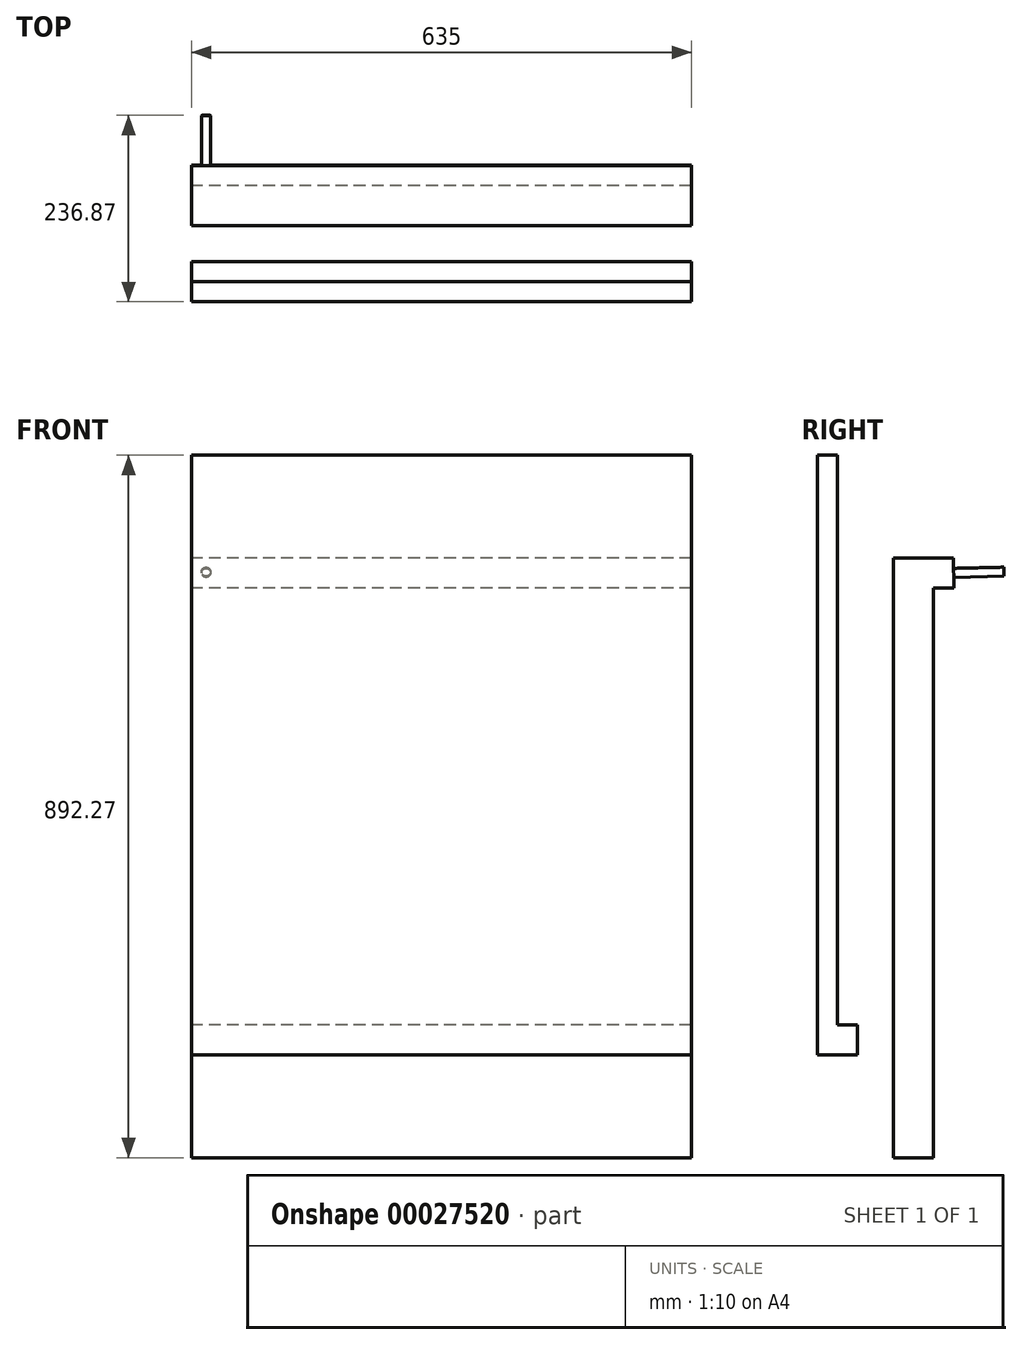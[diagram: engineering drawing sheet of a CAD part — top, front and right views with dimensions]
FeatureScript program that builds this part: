
annotation { "Feature Type Name" : "Feature", "Feature Type Description" : "" }
export const myFeature = defineFeature(function(context is Context, id is Id, definition is map)
    precondition{}
    {
        {
            var Q0;
            Q0=qCreatedBy(makeId("Right.planeOp"),FACE);
            var sketch = newSketch(context, id + "F0", { "sketchPlane" : qUnion([Q0])});
            skLineSegment(sketch, "E0", {"start": v(-59.04, 414.09) * mm, "end": v(-59.04, -347.91) * mm});
            skLineSegment(sketch, "E1", {"start": v(-8.24, -347.91) * mm, "end": v(-8.24, 375.99) * mm});
            skLineSegment(sketch, "E2", {"start": v(-8.24, 375.99) * mm, "end": v(18.02, 375.99) * mm});
            skLineSegment(sketch, "E3", {"start": v(17.16, 414.09) * mm, "end": v(18.02, 375.99) * mm});
            skLineSegment(sketch, "E4", {"start": v(-59.04, -347.91) * mm, "end": v(-8.24, -347.91) * mm});
            skLineSegment(sketch, "E5", {"start": v(-59.04, 414.09) * mm, "end": v(17.16, 414.09) * mm});
            skSolve(sketch);
        }
        {
            var Q0;
            Q0=makeQuery(id+"F0.imprint","IMPRINT",FACE,{"disambiguationData":[TD([[makeQuery(id+"F0.imprint","IMPRINT",EDGE,{"derivedFrom":sQuery(id+"F0.wireOp",EDGE,"E0")}),1.0]])]});
            extrude(context, id + "F1", {"entities" : qUnion([Q0]), "depth" : 635 * mm});
        }
        {
            var Q0;
            Q0=qCreatedBy(makeId("Right.planeOp"),FACE);
            var sketch = newSketch(context, id + "F2", { "sketchPlane" : qUnion([Q0])});
            skLineSegment(sketch, "E6", {"start": v(-155.67, 544.36) * mm, "end": v(-155.67, -217.64) * mm});
            skLineSegment(sketch, "E7", {"start": v(-155.67, -217.64) * mm, "end": v(-104.87, -217.64) * mm});
            skLineSegment(sketch, "E8", {"start": v(-104.87, -217.64) * mm, "end": v(-104.87, -179.54) * mm});
            skLineSegment(sketch, "E9", {"start": v(-104.87, -179.54) * mm, "end": v(-130.27, -179.54) * mm});
            skLineSegment(sketch, "E10", {"start": v(-130.27, -179.54) * mm, "end": v(-130.27, 518.96) * mm});
            skLineSegment(sketch, "E11", {"start": v(-130.27, 518.96) * mm, "end": v(-130.27, 518.96) * mm});
            skLineSegment(sketch, "E12", {"start": v(-130.27, 518.96) * mm, "end": v(-130.27, 544.36) * mm});
            skLineSegment(sketch, "E13", {"start": v(-130.27, 544.36) * mm, "end": v(-155.67, 544.36) * mm});
            skSolve(sketch);
        }
        {
            var Q0;
            Q0=makeQuery(id+"F2.imprint","IMPRINT",FACE,{"disambiguationData":[TD([[makeQuery(id+"F2.imprint","IMPRINT",EDGE,{"derivedFrom":sQuery(id+"F2.wireOp",EDGE,"E6")}),1.0]])]});
            extrude(context, id + "F3", {"entities" : qUnion([Q0]), "depth" : 635 * mm});
        }
        {
            var Q0;
            Q0=makeQuery(id+"F1.opExtrude","SWEPT_FACE",FACE,{"disambiguationData":[OSD([sQuery(id+"F0.wireOp",EDGE,"E3")])]});
            var sketch = newSketch(context, id + "F4", { "sketchPlane" : qUnion([Q0])});
            skCircle(sketch, "E14", {"center": v(-18.41, 394.55) * mm, "radius": 5.72 * mm});
            skSolve(sketch);
        }
        {
            var Q0;
            Q0=makeQuery(id+"F4.imprint","IMPRINT",FACE,{"disambiguationData":[TD([[makeQuery(id+"F4.imprint","IMPRINT",EDGE,{"derivedFrom":sQuery(id+"F4.wireOp",EDGE,"E14")}),1.0]])]});
            extrude(context, id + "F5", {"entities" : qUnion([Q0]), "operationType" : NewBodyOperationType.ADD, "depth" : 63.5 * mm});
        }
    });
